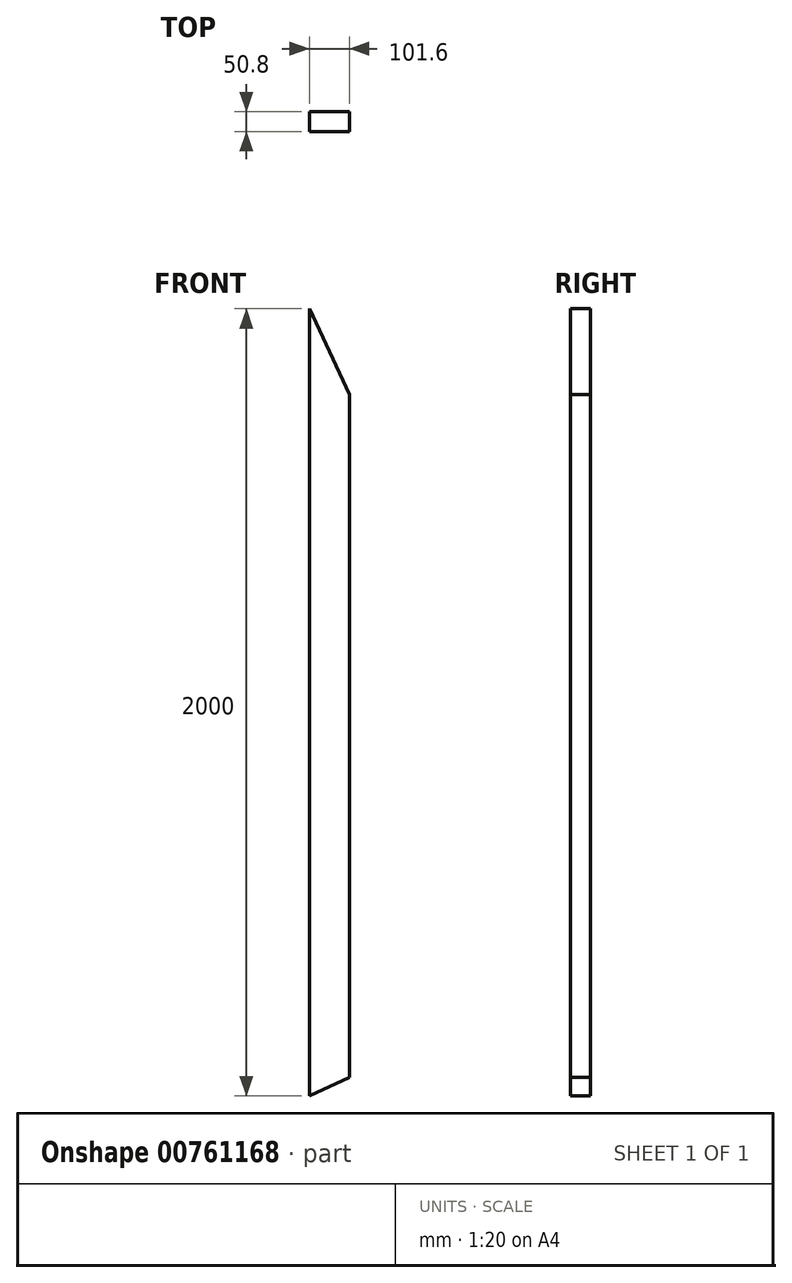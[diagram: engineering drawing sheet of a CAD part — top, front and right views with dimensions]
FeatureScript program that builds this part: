
annotation { "Feature Type Name" : "Feature", "Feature Type Description" : "" }
export const myFeature = defineFeature(function(context is Context, id is Id, definition is map)
    precondition{}
    {
        {
            var Q0;
            Q0=qCreatedBy(makeId("Front.planeOp"),FACE);
            var sketch = newSketch(context, id + "F0", { "sketchPlane" : qUnion([Q0])});
            skLineSegment(sketch, "E0.left", {"start": v(-110.93, -1000.81) * mm, "end": v(-110.93, 999.19) * mm});
            skLineSegment(sketch, "E0.right", {"start": v(-9.33, -953.44) * mm, "end": v(-9.33, 781.3) * mm});
            skLineSegment(sketch, "E1", {"start": v(-110.93, -1000.81) * mm, "end": v(-9.33, -953.44) * mm});
            skLineSegment(sketch, "E2", {"start": v(-110.93, 999.19) * mm, "end": v(-9.33, 781.3) * mm});
            skSolve(sketch);
        }
        {
            var Q0;
            Q0=makeQuery(id+"F0.imprint","IMPRINT",FACE,{"disambiguationData":[TD([[makeQuery(id+"F0.imprint","IMPRINT",EDGE,{"derivedFrom":sQuery(id+"F0.wireOp",EDGE,"E0.left")}),-1.0]])]});
            extrude(context, id + "F1", {"entities" : qUnion([Q0]), "depth" : 50.8 * mm, "offsetDistance" : 25.4 * mm});
        }
    });
